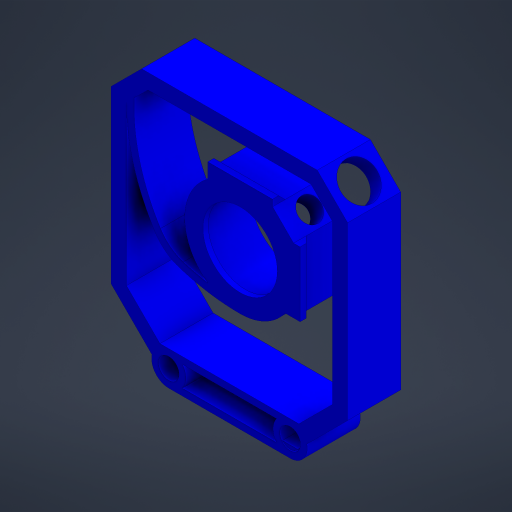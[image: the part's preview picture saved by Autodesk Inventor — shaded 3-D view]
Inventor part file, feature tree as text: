
AUTODESK INVENTOR PART (.ipt)
format: ipt  version: 2023.4 (Build 274418000, 418)  size: 506,368 bytes
history: native  units: mm
features: extrude x6, projected_geometry x4, reference x4, other x3, plane x1, mirror x1, sketch x1
ambient origin geometry x8: Origin, YZ Plane, XZ Plane, XY Plane, X Axis, Y Axis, Z Axis, Center Point
bodies: Solid1 (feature_tree)
feature tree (20):
  extrude  "Extrusion1"  TaperAngle=45.0deg  [1 undecoded]
  extrude  "Extrusion2"  Depth=10.0mm
  extrude  "Extrusion3"  Depth=10.0mm
  extrude  "Extrusion4"  Depth=10.0mm
  plane  "Work Plane1"
  mirror  "Mirror1"
  extrude  "Extrusion5"  Depth=10.0mm
  extrude  "Extrusion6"  Depth=10.0mm
  sketch  "Sketch1"  dims[d2=2.5mm d3=45.0deg d4=14.0mm d5=0.675mm d6=2.125mm d7=0.5mm d8=10.675mm d9=2.5mm d10=0.625mm d11=5.0mm d12=135.0deg d13=3.0mm d14=2.0mm d15=2.0mm d16=38.935534mm d17=38.935534mm d18=9.25mm d19=9.25mm d20=9.25mm d21=9.25mm d22=5.0mm d23=5.0mm d24=5.0mm d25=5.0mm d26=2.5mm d28=8.75mm d29=0.0mm d30=0.875mm d31=0.875mm d32=0.0mm d33=5.75mm d34=10.0mm d35=0.0mm d36=1.0mm d37=135.0deg d38=10.0mm d39=0.0mm d40=3.75mm d41=6.0mm d42=5.0mm d43=0.0mm d44=10.0mm d45=0.0mm d46=2.5mm d50=12.5mm d51=2.5mm d52=1.25mm d53=2.5mm d54=2.5mm d61=1.25mm d62=1.25mm d63=0.1425mm d64=0.1425mm]
  projected_geometry  "Projected Loop1"
  projected_geometry  "Projected Loop2"
  projected_geometry  "Projected Loop4"
  projected_geometry  "Projected Loop5"
  reference  "Reference4"
  reference  "Reference5"
  reference  "Reference6"
  reference  "Reference7"
  other  "<path>\Projects\Project Protocube\Protocube\CAD, STL, OBJ Files\1 CAD\Cube 1x1 V5.iam"
  other  "Cube 1x1 V5.iam"
  other  "Cube 1x1 Bottom V5 Closed Slotted:1"
note: 1 required parameter value undecoded (feature->parameter linkage not recoverable at this tier; creation-order binding heuristic only, values carry confidence <= 0.55)
note: 1 file-system path scrubbed to <path> (originals preserved in map.json)
